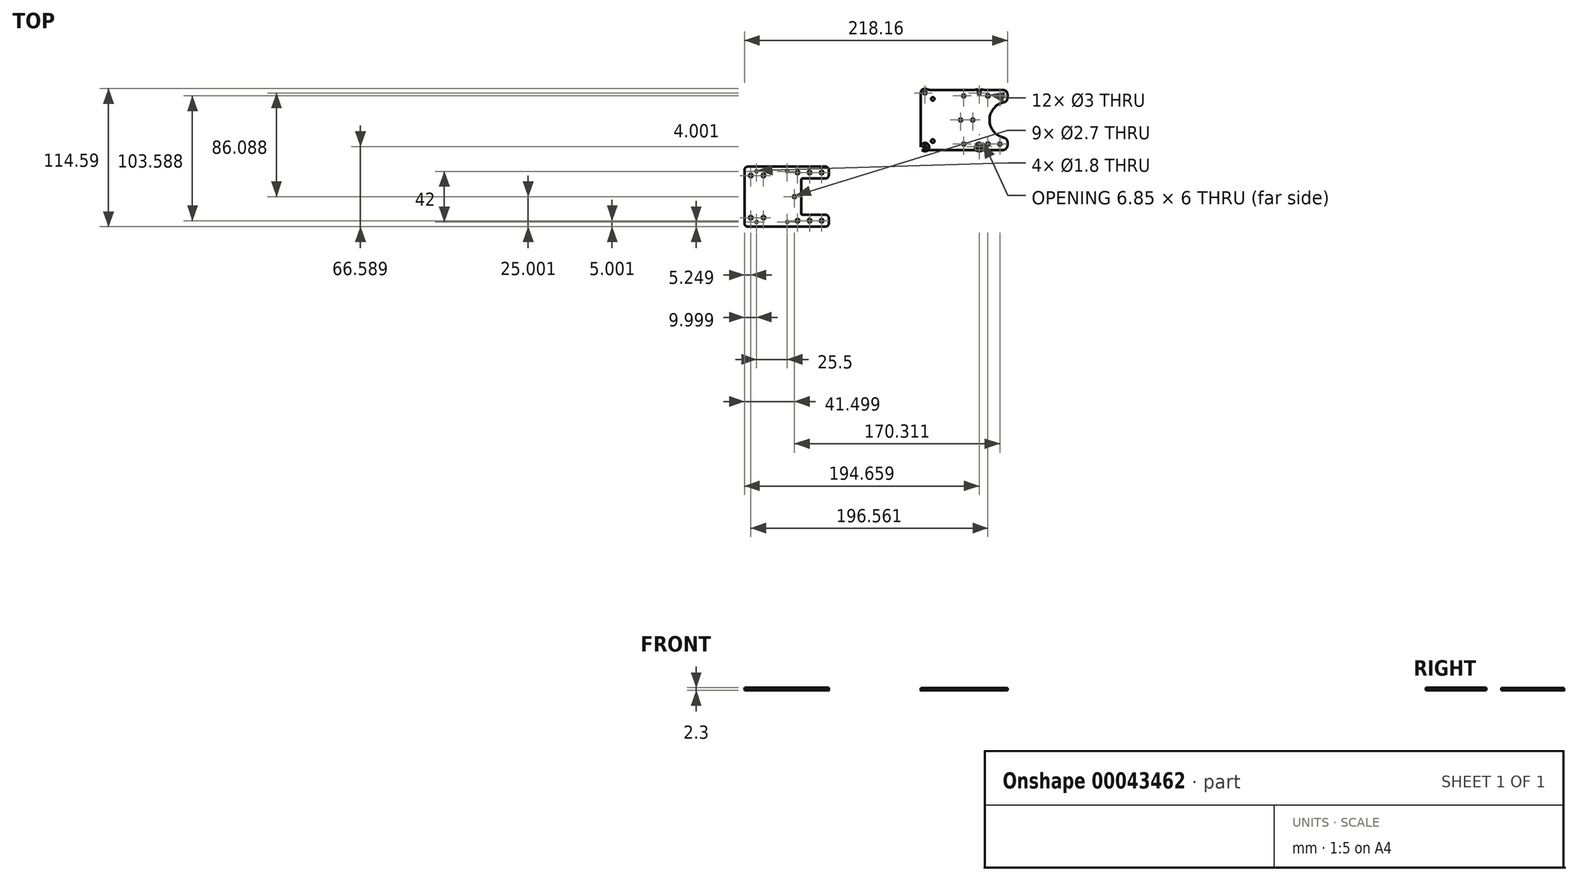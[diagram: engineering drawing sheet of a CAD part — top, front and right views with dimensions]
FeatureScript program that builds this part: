
annotation { "Feature Type Name" : "Feature", "Feature Type Description" : "" }
export const myFeature = defineFeature(function(context is Context, id is Id, definition is map)
    precondition{}
    {
        {
            var Q0;
            Q0=qCreatedBy(makeId("Top.planeOp"),FACE);
            var sketch = newSketch(context, id + "F0", { "sketchPlane" : qUnion([Q0])});
            skLineSegment(sketch, "E0", {"start": v(-156.87, 100.23) * mm, "end": v(-220.87, 100.23) * mm});
            skLineSegment(sketch, "E1", {"start": v(-223.87, 97.23) * mm, "end": v(-223.87, 53.23) * mm});
            skLineSegment(sketch, "E2", {"start": v(-220.87, 50.23) * mm, "end": v(-156.87, 50.23) * mm});
            skLineSegment(sketch, "E3", {"start": v(-153.87, 53.23) * mm, "end": v(-153.87, 57.23) * mm});
            skLineSegment(sketch, "E4", {"start": v(-156.87, 60.23) * mm, "end": v(-175.87, 60.23) * mm});
            skLineSegment(sketch, "E5", {"start": v(-176.87, 61.23) * mm, "end": v(-176.87, 89.23) * mm});
            skLineSegment(sketch, "E6", {"start": v(-175.87, 90.23) * mm, "end": v(-156.87, 90.23) * mm});
            skLineSegment(sketch, "E7", {"start": v(-153.87, 93.23) * mm, "end": v(-153.87, 97.23) * mm});
            skCircle(sketch, "E8", {"center": v(-179.87, 95.23) * mm, "radius": 1.5 * mm});
            skCircle(sketch, "E9", {"center": v(-159.87, 95.23) * mm, "radius": 1.5 * mm});
            skLineSegment(sketch, "E10", {"start": v(-176.87, 75.23) * mm, "end": v(-140.11, 75.23) * mm});
            skCircle(sketch, "E11.MirrorC", {"center": v(-179.87, 55.23) * mm, "radius": 1.5 * mm});
            skCircle(sketch, "E12", {"center": v(-218.62, 92.73) * mm, "radius": 1.5 * mm});
            skCircle(sketch, "E13", {"center": v(-208.12, 92.73) * mm, "radius": 1.5 * mm});
            skCircle(sketch, "E14.MirrorC", {"center": v(-218.62, 57.73) * mm, "radius": 1.5 * mm});
            skCircle(sketch, "E15.MirrorC", {"center": v(-208.12, 57.73) * mm, "radius": 1.5 * mm});
            skPoint(sketch, "E16.visualSharp", {"position": v(-153.87, 100.23) * mm});
            skArc(sketch, "E16.filletArc", {"start": v(-153.87, 97.23) * mm, "mid": v(-154.75, 99.35) * mm, "end": v(-156.87, 100.23) * mm});
            skPoint(sketch, "E17.visualSharp", {"position": v(-153.87, 90.23) * mm});
            skArc(sketch, "E17.filletArc", {"start": v(-156.87, 90.23) * mm, "mid": v(-154.75, 91.1) * mm, "end": v(-153.87, 93.23) * mm});
            skPoint(sketch, "E18.visualSharp", {"position": v(-176.87, 90.23) * mm});
            skArc(sketch, "E18.filletArc", {"start": v(-175.87, 90.23) * mm, "mid": v(-176.58, 89.94) * mm, "end": v(-176.87, 89.23) * mm});
            skPoint(sketch, "E19.visualSharp", {"position": v(-176.87, 60.23) * mm});
            skArc(sketch, "E19.filletArc", {"start": v(-176.87, 61.23) * mm, "mid": v(-176.58, 60.52) * mm, "end": v(-175.87, 60.23) * mm});
            skPoint(sketch, "E20.visualSharp", {"position": v(-153.87, 60.23) * mm});
            skArc(sketch, "E20.filletArc", {"start": v(-153.87, 57.23) * mm, "mid": v(-154.75, 59.35) * mm, "end": v(-156.87, 60.23) * mm});
            skPoint(sketch, "E21.visualSharp", {"position": v(-153.87, 50.23) * mm});
            skArc(sketch, "E21.filletArc", {"start": v(-156.87, 50.23) * mm, "mid": v(-154.75, 51.1) * mm, "end": v(-153.87, 53.23) * mm});
            skPoint(sketch, "E22.visualSharp", {"position": v(-223.87, 50.23) * mm});
            skArc(sketch, "E22.filletArc", {"start": v(-223.87, 53.23) * mm, "mid": v(-223, 51.1) * mm, "end": v(-220.87, 50.23) * mm});
            skPoint(sketch, "E23.visualSharp", {"position": v(-223.87, 100.23) * mm});
            skArc(sketch, "E23.filletArc", {"start": v(-220.87, 100.23) * mm, "mid": v(-223, 99.35) * mm, "end": v(-223.87, 97.23) * mm});
            skCircle(sketch, "E24", {"center": v(-213.87, 96.23) * mm, "radius": 0.9 * mm});
            skCircle(sketch, "E25", {"center": v(-188.37, 96.23) * mm, "radius": 0.9 * mm});
            skCircle(sketch, "E26", {"center": v(-188.37, 54.23) * mm, "radius": 0.9 * mm});
            skCircle(sketch, "E27", {"center": v(-213.87, 54.23) * mm, "radius": 0.9 * mm});
            skCircle(sketch, "E28", {"center": v(-221.37, 87.48) * mm, "radius": 0.9 * mm});
            skCircle(sketch, "E29", {"center": v(-179.37, 87.48) * mm, "radius": 0.9 * mm});
            skCircle(sketch, "E30", {"center": v(-179.37, 61.98) * mm, "radius": 0.9 * mm});
            skCircle(sketch, "E31", {"center": v(-221.37, 61.98) * mm, "radius": 0.9 * mm});
            skCircle(sketch, "E32", {"center": v(-220.52, 75.23) * mm, "radius": 1.35 * mm});
            skArc(sketch, "E33", {"start": v(-224.54, 98.09) * mm, "mid": v(-227.87, 75.23) * mm, "end": v(-224.54, 52.37) * mm});
            skLineSegment(sketch, "E34", {"start": v(-221.67, 100.23) * mm, "end": v(-220.87, 100.23) * mm});
            skLineSegment(sketch, "E35", {"start": v(-221.67, 50.23) * mm, "end": v(-220.87, 50.23) * mm});
            skArc(sketch, "E36.filletArc", {"start": v(-221.67, 100.23) * mm, "mid": v(-223.46, 99.64) * mm, "end": v(-224.54, 98.09) * mm});
            skArc(sketch, "E37.filletArc", {"start": v(-224.54, 52.37) * mm, "mid": v(-223.46, 50.83) * mm, "end": v(-221.67, 50.23) * mm});
            skCircle(sketch, "E38.MirrorC", {"center": v(-169.87, 95.23) * mm, "radius": 1.5 * mm});
            skCircle(sketch, "E39", {"center": v(-182.37, 75.23) * mm, "radius": 1.35 * mm});
            skCircle(sketch, "E40.MirrorC", {"center": v(-169.87, 55.23) * mm, "radius": 1.5 * mm});
            skCircle(sketch, "E41.MirrorC", {"center": v(-159.87, 55.23) * mm, "radius": 1.5 * mm});
            skSolve(sketch);
        }
        {
            var Q0;
            Q0=makeQuery(id+"F0.imprint","IMPRINT",FACE,{"disambiguationData":[TD([[makeQuery(id+"F0.imprint","IMPRINT",EDGE,{"derivedFrom":sQuery(id+"F0.wireOp",EDGE,"E0")}),1.0]])]});
            var Q1;
            Q1=makeQuery(id+"F0.imprint","IMPRINT",FACE,{"disambiguationData":[TD([[makeQuery(id+"F0.imprint","IMPRINT",EDGE,{"derivedFrom":sQuery(id+"F0.wireOp",EDGE,"E0")}),1.0]])]});
            var Q2;
            Q2=makeQuery(id+"F0.imprint","IMPRINT",FACE,{"disambiguationData":[TD([[makeQuery(id+"F0.imprint","IMPRINT",EDGE,{"derivedFrom":sQuery(id+"F0.wireOp",EDGE,"E0")}),1.0]])]});
            var Q3;
            Q3=makeQuery(id+"F0.imprint","IMPRINT",FACE,{"disambiguationData":[TD([[makeQuery(id+"F0.imprint","IMPRINT",EDGE,{"derivedFrom":sQuery(id+"F0.wireOp",EDGE,"E0")}),1.0]])]});
            var Q4;
            Q4=makeQuery(id+"F0.imprint","IMPRINT",FACE,{"disambiguationData":[TD([[makeQuery(id+"F0.imprint","IMPRINT",EDGE,{"derivedFrom":sQuery(id+"F0.wireOp",EDGE,"E0")}),1.0]])]});
            var Q5;
            Q5=makeQuery(id+"F0.imprint","IMPRINT",FACE,{"disambiguationData":[TD([[makeQuery(id+"F0.imprint","IMPRINT",EDGE,{"derivedFrom":sQuery(id+"F0.wireOp",EDGE,"E28")}),1.0]])]});
            var Q6;
            Q6=makeQuery(id+"F0.imprint","IMPRINT",FACE,{"disambiguationData":[TD([[makeQuery(id+"F0.imprint","IMPRINT",EDGE,{"derivedFrom":sQuery(id+"F0.wireOp",EDGE,"E29")}),1.0]])]});
            var Q7;
            Q7=makeQuery(id+"F0.imprint","IMPRINT",FACE,{"disambiguationData":[TD([[makeQuery(id+"F0.imprint","IMPRINT",EDGE,{"derivedFrom":sQuery(id+"F0.wireOp",EDGE,"E30")}),1.0]])]});
            var Q8;
            Q8=makeQuery(id+"F0.imprint","IMPRINT",FACE,{"disambiguationData":[TD([[makeQuery(id+"F0.imprint","IMPRINT",EDGE,{"derivedFrom":sQuery(id+"F0.wireOp",EDGE,"E31")}),1.0]])]});
            var Q9;
            Q9=makeQuery(id+"F0.imprint","IMPRINT",FACE,{"disambiguationData":[TD([[makeQuery(id+"F0.imprint","IMPRINT",EDGE,{"derivedFrom":sQuery(id+"F0.wireOp",EDGE,"E32")}),1.0]])]});
            var Q10;
            {var subQ0=sQuery(id+"F0.wireOp",EDGE,"E18.filletArc");Q10=makeQuery(id+"F0.imprint","IMPRINT",FACE,{"disambiguationData":[TD([[makeQuery(id+"F0.imprint","IMPRINT",EDGE,{"derivedFrom":subQ0}),1.0]])]});}
            var Q11;
            {var subQ0=sQuery(id+"F0.wireOp",EDGE,"E19.filletArc");Q11=makeQuery(id+"F0.imprint","IMPRINT",FACE,{"disambiguationData":[TD([[makeQuery(id+"F0.imprint","IMPRINT",EDGE,{"derivedFrom":subQ0}),1.0]])]});}
            extrude(context, id + "F1", {"entities" : qUnion([Q0, Q1, Q2, Q3, Q4, Q5, Q6, Q7, Q8, Q9, Q10, Q11]), "depth" : 2.3 * mm});
        }
        {
            var Q0;
            Q0=qCreatedBy(makeId("Top.planeOp"),FACE);
            var sketch = newSketch(context, id + "F2", { "sketchPlane" : qUnion([Q0])});
            skLineSegment(sketch, "E42", {"start": v(-77.71, 163.82) * mm, "end": v(-9.71, 163.82) * mm});
            skLineSegment(sketch, "E43", {"start": v(-5.71, 159.82) * mm, "end": v(-5.71, 157.4) * mm});
            skLineSegment(sketch, "E44", {"start": v(-5.71, 153.82) * mm, "end": v(-20.71, 153.82) * mm});
            skLineSegment(sketch, "E45", {"start": v(-20.71, 153.82) * mm, "end": v(-20.71, 123.82) * mm});
            skLineSegment(sketch, "E46", {"start": v(-20.71, 123.82) * mm, "end": v(-5.71, 123.82) * mm});
            skLineSegment(sketch, "E47", {"start": v(-5.71, 120.24) * mm, "end": v(-5.71, 117.82) * mm});
            skLineSegment(sketch, "E48", {"start": v(-9.71, 113.82) * mm, "end": v(-77.71, 113.82) * mm});
            skLineSegment(sketch, "E49", {"start": v(-77.71, 113.82) * mm, "end": v(-77.71, 163.82) * mm});
            skCircle(sketch, "E50", {"center": v(-12.06, 158.82) * mm, "radius": 1.35 * mm});
            skCircle(sketch, "E51", {"center": v(-22.06, 158.82) * mm, "radius": 1.5 * mm});
            skCircle(sketch, "E52", {"center": v(-42.06, 158.82) * mm, "radius": 1.35 * mm});
            skCircle(sketch, "E53", {"center": v(-67.71, 156.32) * mm, "radius": 1.45 * mm});
            skLineSegment(sketch, "E54", {"start": v(-77.71, 138.82) * mm, "end": v(-20.71, 138.82) * mm});
            skCircle(sketch, "E55", {"center": v(-74.21, 161.32) * mm, "radius": 1.35 * mm});
            skCircle(sketch, "E56", {"center": v(-74.21, 161.32) * mm, "radius": 3.5 * mm});
            skCircle(sketch, "E57", {"center": v(-29.21, 161.32) * mm, "radius": 1.35 * mm});
            skCircle(sketch, "E58", {"center": v(-29.21, 161.32) * mm, "radius": 3.5 * mm});
            skCircle(sketch, "E59", {"center": v(-70.21, 168.82) * mm, "radius": 5 * mm});
            skCircle(sketch, "E60", {"center": v(-33.21, 168.82) * mm, "radius": 5 * mm});
            skCircle(sketch, "E61", {"center": v(-25.21, 168.82) * mm, "radius": 5 * mm});
            skArc(sketch, "E62", {"start": v(-8.87, 153.48) * mm, "mid": v(-20.71, 138.82) * mm, "end": v(-8.87, 124.15) * mm});
            skPoint(sketch, "E63.visualSharp", {"position": v(-5.71, 163.82) * mm});
            skArc(sketch, "E63.filletArc", {"start": v(-5.71, 159.82) * mm, "mid": v(-6.88, 162.65) * mm, "end": v(-9.71, 163.82) * mm});
            skPoint(sketch, "E64.visualSharp", {"position": v(-5.71, 153.82) * mm});
            skArc(sketch, "E64.filletArc", {"start": v(-8.87, 153.48) * mm, "mid": v(-6.6, 154.88) * mm, "end": v(-5.71, 157.4) * mm});
            skPoint(sketch, "E65.visualSharp", {"position": v(-5.71, 123.82) * mm});
            skArc(sketch, "E65.filletArc", {"start": v(-5.71, 120.24) * mm, "mid": v(-6.6, 122.76) * mm, "end": v(-8.87, 124.15) * mm});
            skPoint(sketch, "E66.visualSharp", {"position": v(-5.71, 113.82) * mm});
            skArc(sketch, "E66.filletArc", {"start": v(-9.71, 113.82) * mm, "mid": v(-6.88, 115) * mm, "end": v(-5.71, 117.82) * mm});
            skCircle(sketch, "E67.MirrorC", {"center": v(-42.06, 118.82) * mm, "radius": 1.35 * mm});
            skCircle(sketch, "E68.MirrorC", {"center": v(-67.71, 121.32) * mm, "radius": 1.45 * mm});
            skCircle(sketch, "E69.MirrorC", {"center": v(-74.21, 116.32) * mm, "radius": 1.35 * mm});
            skCircle(sketch, "E70.MirrorC", {"center": v(-74.21, 116.32) * mm, "radius": 3.5 * mm});
            skCircle(sketch, "E71.MirrorC", {"center": v(-25.21, 108.82) * mm, "radius": 5 * mm});
            skCircle(sketch, "E72.MirrorC", {"center": v(-29.21, 116.32) * mm, "radius": 3.5 * mm});
            skCircle(sketch, "E73.MirrorC", {"center": v(-70.21, 108.82) * mm, "radius": 5 * mm});
            skCircle(sketch, "E74.MirrorC", {"center": v(-33.21, 108.82) * mm, "radius": 5 * mm});
            skCircle(sketch, "E75.MirrorC", {"center": v(-29.21, 116.32) * mm, "radius": 1.35 * mm});
            skCircle(sketch, "E76.MirrorC", {"center": v(-22.06, 118.82) * mm, "radius": 1.5 * mm});
            skCircle(sketch, "E77.MirrorC", {"center": v(-12.06, 118.82) * mm, "radius": 1.35 * mm});
            skCircle(sketch, "E78", {"center": v(-44.56, 138.82) * mm, "radius": 1.35 * mm});
            skCircle(sketch, "E79", {"center": v(-34.56, 138.82) * mm, "radius": 1.35 * mm});
            skSolve(sketch);
        }
        {
            var Q0;
            {var subQ0=sQuery(id+"F2.wireOp",EDGE,"E45");var subQ1=sQuery(id+"F2.wireOp",EDGE,"E44");var subQ2=makeQuery(id+"F2.imprint","INTERSECT",VERTEX,{"derivedFrom":[subQ1,subQ0]});Q0=makeQuery(id+"F2.imprint","IMPRINT",FACE,{"disambiguationData":[TD([[makeQuery(id+"F2.imprint","IMPRINT",EDGE,{"disambiguationData":[TD([[subQ2,1.0]])],"derivedFrom":subQ1}),1.0]])]});}
            var Q1;
            {var subQ0=sQuery(id+"F2.wireOp",EDGE,"E46");var subQ1=sQuery(id+"F2.wireOp",EDGE,"E45");var subQ2=makeQuery(id+"F2.imprint","INTERSECT",VERTEX,{"derivedFrom":[subQ1,subQ0]});Q1=makeQuery(id+"F2.imprint","IMPRINT",FACE,{"disambiguationData":[TD([[makeQuery(id+"F2.imprint","IMPRINT",EDGE,{"disambiguationData":[TD([[subQ2,-1.0]])],"derivedFrom":subQ0}),1.0]])]});}
            var Q2;
            {var subQ0=sQuery(id+"F2.wireOp",EDGE,"E56");var subQ1=sQuery(id+"F2.wireOp",EDGE,"E42");var subQ2=makeQuery(id+"F2.imprint","INTERSECT",VERTEX,{"disambiguationData":[OD(0.0)],"derivedFrom":[subQ1,subQ0]});Q2=makeQuery(id+"F2.imprint","IMPRINT",FACE,{"disambiguationData":[TD([[makeQuery(id+"F2.imprint","IMPRINT",EDGE,{"disambiguationData":[TD([[subQ2,-1.0]])],"derivedFrom":subQ1}),1.0]])]});}
            var Q3;
            {var subQ0=sQuery(id+"F2.wireOp",EDGE,"E70.MirrorC");var subQ1=sQuery(id+"F2.wireOp",EDGE,"E48");var subQ2=makeQuery(id+"F2.imprint","INTERSECT",VERTEX,{"disambiguationData":[OD(0.0)],"derivedFrom":[subQ1,subQ0]});Q3=makeQuery(id+"F2.imprint","IMPRINT",FACE,{"disambiguationData":[TD([[makeQuery(id+"F2.imprint","IMPRINT",EDGE,{"disambiguationData":[TD([[subQ2,1.0]])],"derivedFrom":subQ1}),1.0]])]});}
            var Q4;
            {var subQ0=sQuery(id+"F2.wireOp",EDGE,"E59");var subQ1=sQuery(id+"F2.wireOp",EDGE,"E42");var subQ2=makeQuery(id+"F2.imprint","INTERSECT",VERTEX,{"derivedFrom":[subQ1,subQ0]});Q4=makeQuery(id+"F2.imprint","IMPRINT",FACE,{"disambiguationData":[TD([[makeQuery(id+"F2.imprint","IMPRINT",EDGE,{"disambiguationData":[TD([[subQ2,1.0]])],"derivedFrom":subQ1}),1.0]])]});}
            var Q5;
            {var subQ0=sQuery(id+"F2.wireOp",EDGE,"E60");var subQ1=sQuery(id+"F2.wireOp",EDGE,"E42");var subQ2=makeQuery(id+"F2.imprint","INTERSECT",VERTEX,{"derivedFrom":[subQ1,subQ0]});Q5=makeQuery(id+"F2.imprint","IMPRINT",FACE,{"disambiguationData":[TD([[makeQuery(id+"F2.imprint","IMPRINT",EDGE,{"disambiguationData":[TD([[subQ2,-1.0]])],"derivedFrom":subQ1}),1.0]])]});}
            var Q6;
            {var subQ0=sQuery(id+"F2.wireOp",EDGE,"E58");var subQ1=sQuery(id+"F2.wireOp",EDGE,"E42");var subQ2=makeQuery(id+"F2.imprint","INTERSECT",VERTEX,{"disambiguationData":[OD(0.0)],"derivedFrom":[subQ1,subQ0]});Q6=makeQuery(id+"F2.imprint","IMPRINT",FACE,{"disambiguationData":[TD([[makeQuery(id+"F2.imprint","IMPRINT",EDGE,{"disambiguationData":[TD([[subQ2,-1.0]])],"derivedFrom":subQ1}),1.0]])]});}
            var Q7;
            {var subQ0=sQuery(id+"F2.wireOp",EDGE,"E61");var subQ1=sQuery(id+"F2.wireOp",EDGE,"E42");var subQ2=makeQuery(id+"F2.imprint","INTERSECT",VERTEX,{"derivedFrom":[subQ1,subQ0]});Q7=makeQuery(id+"F2.imprint","IMPRINT",FACE,{"disambiguationData":[TD([[makeQuery(id+"F2.imprint","IMPRINT",EDGE,{"disambiguationData":[TD([[subQ2,1.0]])],"derivedFrom":subQ1}),1.0]])]});}
            var Q8;
            {var subQ0=sQuery(id+"F2.wireOp",EDGE,"E71.MirrorC");var subQ1=sQuery(id+"F2.wireOp",EDGE,"E48");var subQ2=makeQuery(id+"F2.imprint","INTERSECT",VERTEX,{"derivedFrom":[subQ1,subQ0]});Q8=makeQuery(id+"F2.imprint","IMPRINT",FACE,{"disambiguationData":[TD([[makeQuery(id+"F2.imprint","IMPRINT",EDGE,{"disambiguationData":[TD([[subQ2,-1.0]])],"derivedFrom":subQ1}),1.0]])]});}
            var Q9;
            {var subQ0=sQuery(id+"F2.wireOp",EDGE,"E72.MirrorC");var subQ1=sQuery(id+"F2.wireOp",EDGE,"E48");var subQ2=makeQuery(id+"F2.imprint","INTERSECT",VERTEX,{"disambiguationData":[OD(0.0)],"derivedFrom":[subQ1,subQ0]});Q9=makeQuery(id+"F2.imprint","IMPRINT",FACE,{"disambiguationData":[TD([[makeQuery(id+"F2.imprint","IMPRINT",EDGE,{"disambiguationData":[TD([[subQ2,-1.0]])],"derivedFrom":subQ1}),1.0]])]});}
            var Q10;
            {var subQ0=sQuery(id+"F2.wireOp",EDGE,"E74.MirrorC");var subQ1=sQuery(id+"F2.wireOp",EDGE,"E48");var subQ2=makeQuery(id+"F2.imprint","INTERSECT",VERTEX,{"derivedFrom":[subQ1,subQ0]});Q10=makeQuery(id+"F2.imprint","IMPRINT",FACE,{"disambiguationData":[TD([[makeQuery(id+"F2.imprint","IMPRINT",EDGE,{"disambiguationData":[TD([[subQ2,1.0]])],"derivedFrom":subQ1}),1.0]])]});}
            var Q11;
            {var subQ0=sQuery(id+"F2.wireOp",EDGE,"E73.MirrorC");var subQ1=sQuery(id+"F2.wireOp",EDGE,"E48");var subQ2=makeQuery(id+"F2.imprint","INTERSECT",VERTEX,{"derivedFrom":[subQ1,subQ0]});Q11=makeQuery(id+"F2.imprint","IMPRINT",FACE,{"disambiguationData":[TD([[makeQuery(id+"F2.imprint","IMPRINT",EDGE,{"disambiguationData":[TD([[subQ2,-1.0]])],"derivedFrom":subQ1}),1.0]])]});}
            var Q12;
            Q12=makeQuery(id+"F2.imprint","IMPRINT",FACE,{"disambiguationData":[TD([[makeQuery(id+"F2.imprint","IMPRINT",EDGE,{"derivedFrom":sQuery(id+"F2.wireOp",EDGE,"E55")}),-1.0]])]});
            var Q13;
            Q13=makeQuery(id+"F2.imprint","IMPRINT",FACE,{"disambiguationData":[TD([[makeQuery(id+"F2.imprint","IMPRINT",EDGE,{"derivedFrom":sQuery(id+"F2.wireOp",EDGE,"E69.MirrorC")}),1.0]])]});
            var Q14;
            {var subQ6=sQuery(id+"F2.wireOp",EDGE,"E43");Q14=makeQuery(id+"F2.imprint","IMPRINT",FACE,{"disambiguationData":[TD([[makeQuery(id+"F2.imprint","IMPRINT",EDGE,{"derivedFrom":subQ6}),-1.0]])]});}
            var Q15;
            {var subQ18=sQuery(id+"F2.wireOp",EDGE,"E47");Q15=makeQuery(id+"F2.imprint","IMPRINT",FACE,{"disambiguationData":[TD([[makeQuery(id+"F2.imprint","IMPRINT",EDGE,{"derivedFrom":subQ18}),-1.0]])]});}
            var Q16;
            Q16=makeQuery(id+"F2.imprint","IMPRINT",FACE,{"disambiguationData":[TD([[makeQuery(id+"F2.imprint","IMPRINT",EDGE,{"derivedFrom":sQuery(id+"F2.wireOp",EDGE,"E57")}),-1.0]])]});
            var Q17;
            Q17=makeQuery(id+"F2.imprint","IMPRINT",FACE,{"disambiguationData":[TD([[makeQuery(id+"F2.imprint","IMPRINT",EDGE,{"derivedFrom":sQuery(id+"F2.wireOp",EDGE,"E75.MirrorC")}),1.0]])]});
            extrude(context, id + "F3", {"entities" : qUnion([Q0, Q1, Q2, Q3, Q4, Q5, Q6, Q7, Q8, Q9, Q10, Q11, Q12, Q13, Q14, Q15, Q16, Q17]), "depth" : 2 * mm});
        }
    });
